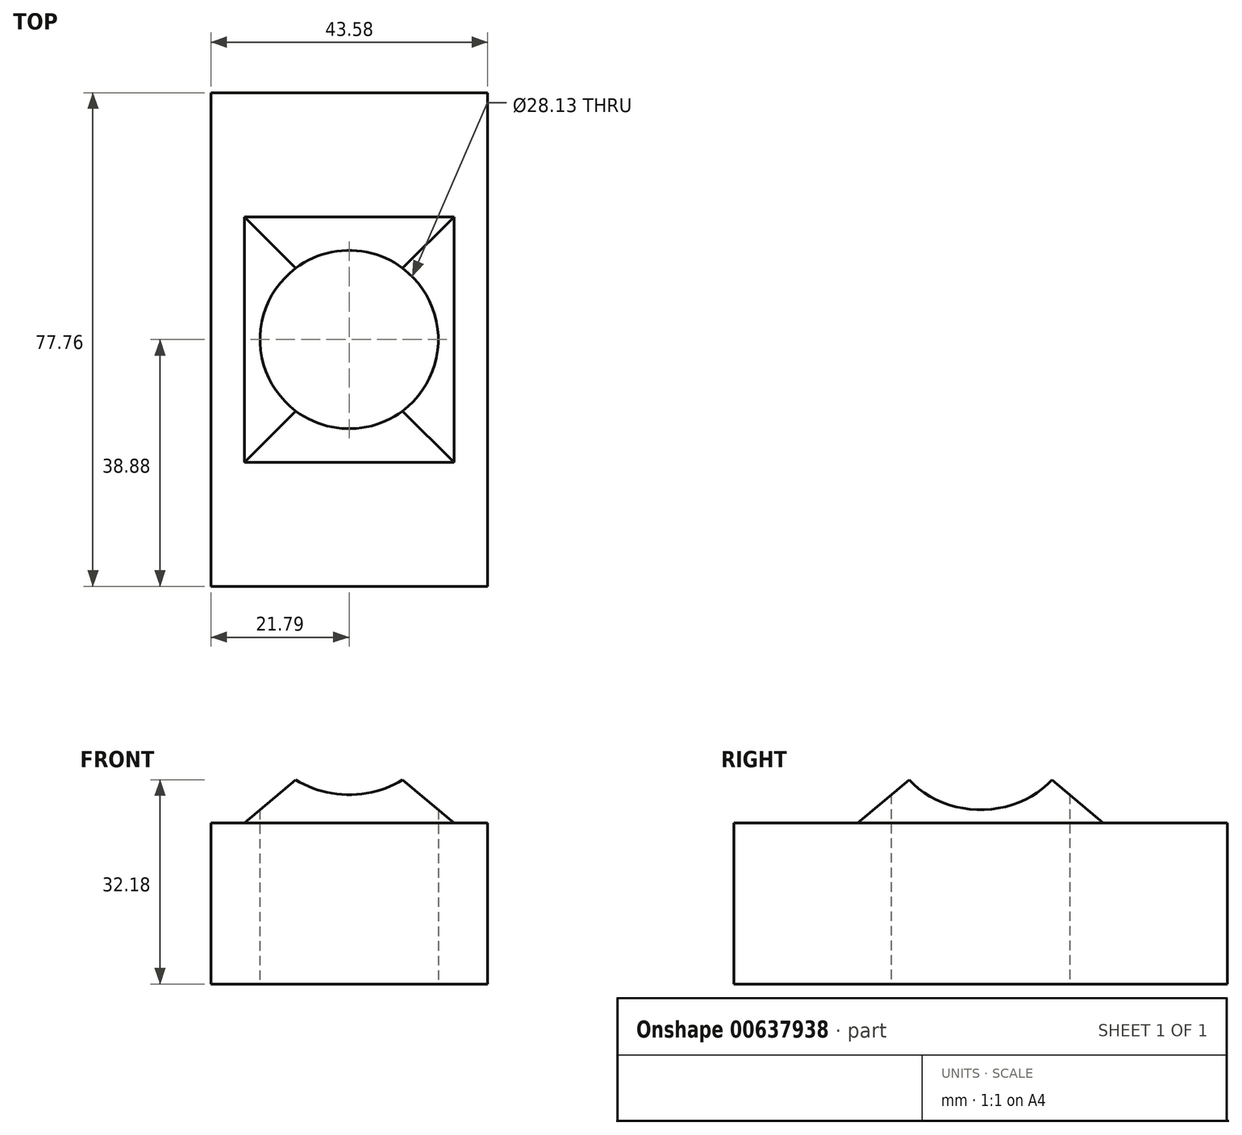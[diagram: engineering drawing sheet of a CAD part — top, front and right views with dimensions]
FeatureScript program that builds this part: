
annotation { "Feature Type Name" : "Feature", "Feature Type Description" : "" }
export const myFeature = defineFeature(function(context is Context, id is Id, definition is map)
    precondition{}
    {
        {
            var Q0;
            Q0=qCreatedBy(makeId("Top.planeOp"),FACE);
            var sketch = newSketch(context, id + "F0", { "sketchPlane" : qUnion([Q0])});
            skLineSegment(sketch, "E0.bottom", {"start": v(21.79, 38.88) * mm, "end": v(-21.79, 38.88) * mm});
            skLineSegment(sketch, "E0.top", {"start": v(21.79, -38.88) * mm, "end": v(-21.79, -38.88) * mm});
            skLineSegment(sketch, "E0.left", {"start": v(21.79, 38.88) * mm, "end": v(21.79, -38.88) * mm});
            skLineSegment(sketch, "E0.right", {"start": v(-21.79, 38.88) * mm, "end": v(-21.79, -38.88) * mm});
            skPoint(sketch, "E0.middle", {"position": v(0, 0) * mm});
            skCircle(sketch, "E1", {"center": v(0, 0) * mm, "radius": 14.06 * mm});
            skSolve(sketch);
        }
        {
            var Q0;
            Q0 = qSketchRegion(id + "F0", true);
            extrude(context, id + "F1", {"entities" : qUnion([Q0]), "depth" : 25.4 * mm, "offsetDistance" : 25.4 * mm});
        }
        {
            var Q0;
            Q0=makeQuery(id+"F1.opExtrude","CAP_FACE",FACE,{"disambiguationData":[OSD([sQuery(id+"F0.wireOp",EDGE,"E0.bottom"),sQuery(id+"F0.wireOp",EDGE,"E0.top"),sQuery(id+"F0.wireOp",EDGE,"E0.left"),sQuery(id+"F0.wireOp",EDGE,"E0.right"),sQuery(id+"F0.wireOp",EDGE,"E1")])],"isStart":false});
            var sketch = newSketch(context, id + "F2", { "sketchPlane" : qUnion([Q0])});
            skLineSegment(sketch, "E2.bottom", {"start": v(16.51, 19.34) * mm, "end": v(-16.51, 19.34) * mm});
            skLineSegment(sketch, "E2.top", {"start": v(16.51, -19.34) * mm, "end": v(-16.51, -19.34) * mm});
            skLineSegment(sketch, "E2.left", {"start": v(16.51, 19.34) * mm, "end": v(16.51, -19.34) * mm});
            skLineSegment(sketch, "E2.right", {"start": v(-16.51, 19.34) * mm, "end": v(-16.51, -19.34) * mm});
            skPoint(sketch, "E2.middle", {"position": v(0, 0) * mm});
            skSolve(sketch);
        }
        {
            var Q0;
            Q0 = qSketchRegion(id + "F2", true);
            extrude(context, id + "F3", {"entities" : qUnion([Q0]), "operationType" : NewBodyOperationType.ADD, "depth" : 25.4 * mm, "offsetDistance" : 25.4 * mm, "hasDraft" : true, "draftAngle" : 50 * degree, "draftPullDirection" : true});
        }
        {
            var Q0;
            Q0=makeQuery(id+"F3.opExtrude","CAP_FACE",FACE,{"disambiguationData":[OSD([sQuery(id+"F2.wireOp",EDGE,"E2.bottom"),sQuery(id+"F2.wireOp",EDGE,"E2.top"),sQuery(id+"F2.wireOp",EDGE,"E2.left"),sQuery(id+"F2.wireOp",EDGE,"E2.right")])],"isStart":true});
            var sketch = newSketch(context, id + "F4", { "sketchPlane" : qUnion([Q0])});
            skCircle(sketch, "E3.0", {"center": v(0, 0) * mm, "radius": 14.06 * mm});
            skSolve(sketch);
        }
        {
            var Q0;
            Q0 = qSketchRegion(id + "F4", true);
            extrude(context, id + "F5", {"entities" : qUnion([Q0]), "operationType" : NewBodyOperationType.REMOVE, "oppositeDirection" : true, "depth" : 25.4 * mm, "offsetDistance" : 25.4 * mm});
        }
    });
